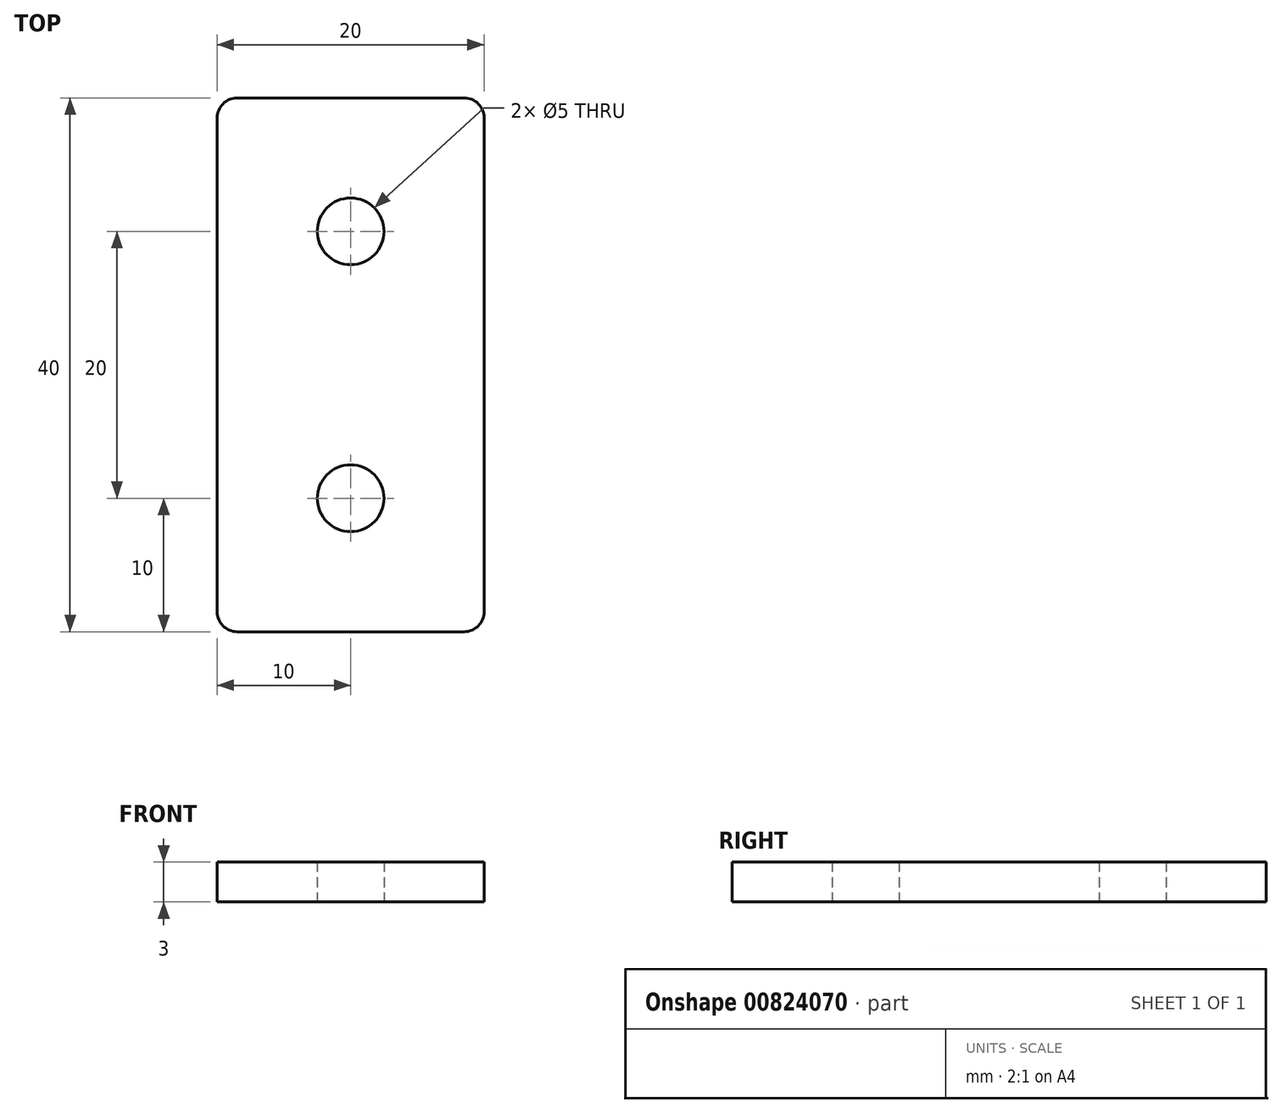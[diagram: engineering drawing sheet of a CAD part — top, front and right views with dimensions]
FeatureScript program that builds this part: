
annotation { "Feature Type Name" : "Feature", "Feature Type Description" : "" }
export const myFeature = defineFeature(function(context is Context, id is Id, definition is map)
    precondition{}
    {
        {
            var Q0;
            Q0=qCreatedBy(makeId("Top.planeOp"),FACE);
            var sketch = newSketch(context, id + "F0", { "sketchPlane" : qUnion([Q0])});
            skLineSegment(sketch, "E0", {"start": v(8.5, -20) * mm, "end": v(-8.5, -20) * mm});
            skLineSegment(sketch, "E1", {"start": v(-10, -18.5) * mm, "end": v(-10, 18.5) * mm});
            skLineSegment(sketch, "E2", {"start": v(10, 18.5) * mm, "end": v(10, -18.5) * mm});
            skLineSegment(sketch, "E3", {"start": v(-8.5, 20) * mm, "end": v(8.5, 20) * mm});
            skCircle(sketch, "E4", {"center": v(0, 10) * mm, "radius": 2.5 * mm});
            skCircle(sketch, "E5", {"center": v(0, -10) * mm, "radius": 2.5 * mm});
            skArc(sketch, "E6", {"start": v(-10, -18.5) * mm, "mid": v(-9.56, -19.56) * mm, "end": v(-8.5, -20) * mm});
            skArc(sketch, "E7", {"start": v(-8.5, 20) * mm, "mid": v(-9.56, 19.56) * mm, "end": v(-10, 18.5) * mm});
            skArc(sketch, "E8", {"start": v(10, 18.5) * mm, "mid": v(9.56, 19.56) * mm, "end": v(8.5, 20) * mm});
            skArc(sketch, "E9", {"start": v(8.5, -20) * mm, "mid": v(9.56, -19.56) * mm, "end": v(10, -18.5) * mm});
            skSolve(sketch);
        }
        {
            var Q0;
            Q0 = qSketchRegion(id + "F0", true);
            extrude(context, id + "F1", {"entities" : qUnion([Q0]), "depth" : 3 * mm, "offsetDistance" : 25 * mm});
        }
    });
